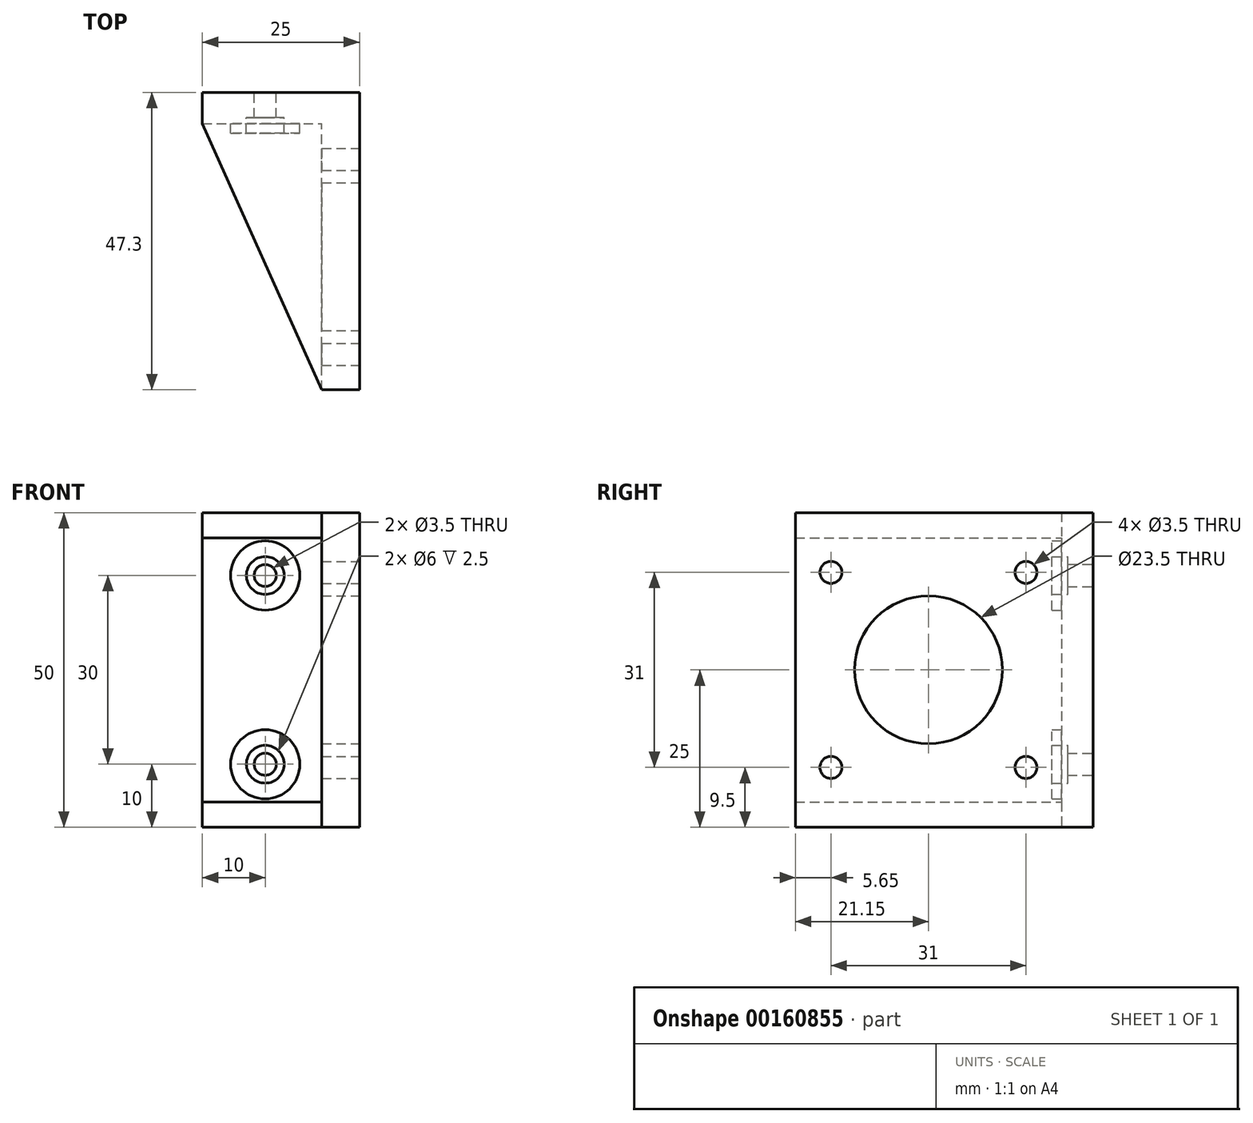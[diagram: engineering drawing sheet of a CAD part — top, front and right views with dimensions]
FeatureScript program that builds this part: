
annotation { "Feature Type Name" : "Feature", "Feature Type Description" : "" }
export const myFeature = defineFeature(function(context is Context, id is Id, definition is map)
    precondition{}
    {
        {
            var Q0;
            Q0=qCreatedBy(makeId("Front.planeOp"),FACE);
            var sketch = newSketch(context, id + "F0", { "sketchPlane" : qUnion([Q0])});
            skCircle(sketch, "E0", {"center": v(0, 15) * mm, "radius": 1.75 * mm});
            skCircle(sketch, "E1.MirrorC", {"center": v(0, -15) * mm, "radius": 1.75 * mm});
            skLineSegment(sketch, "E2.bottom", {"start": v(-10, 25) * mm, "end": v(15, 25) * mm});
            skLineSegment(sketch, "E2.top", {"start": v(-10, -25) * mm, "end": v(15, -25) * mm});
            skLineSegment(sketch, "E2.left", {"start": v(-10, 25) * mm, "end": v(-10, -25) * mm});
            skLineSegment(sketch, "E2.right", {"start": v(15, 25) * mm, "end": v(15, -25) * mm});
            skLineSegment(sketch, "E3", {"start": v(-10, 0) * mm, "end": v(0, 0) * mm});
            skPoint(sketch, "E4.visualSharp", {"position": v(-10, 25) * mm});
            skPoint(sketch, "E5.visualSharp", {"position": v(-10, -25) * mm});
            skSolve(sketch);
        }
        {
            var Q0;
            Q0 = qSketchRegion(id + "F0", true);
            extrude(context, id + "F1", {"entities" : qUnion([Q0]), "depth" : 5 * mm, "offsetDistance" : 25 * mm});
        }
        {
            var Q0;
            Q0=makeQuery(id+"F1.opExtrude","SWEPT_FACE",FACE,{"disambiguationData":[OSD([sQuery(id+"F0.wireOp",EDGE,"E2.right")])]});
            var sketch = newSketch(context, id + "F2", { "sketchPlane" : qUnion([Q0])});
            skLineSegment(sketch, "E6.bottom", {"start": v(-47.3, 25) * mm, "end": v(-5, 25) * mm});
            skLineSegment(sketch, "E6.top", {"start": v(-47.3, -25) * mm, "end": v(-5, -25) * mm});
            skLineSegment(sketch, "E6.left", {"start": v(-47.3, 25) * mm, "end": v(-47.3, -25) * mm});
            skLineSegment(sketch, "E6.right", {"start": v(-5, 25) * mm, "end": v(-5, -25) * mm});
            skLineSegment(sketch, "E7", {"start": v(-5, 0) * mm, "end": v(0, 0) * mm});
            skCircle(sketch, "E8", {"center": v(-26.15, 0) * mm, "radius": 11.75 * mm});
            skLineSegment(sketch, "E9", {"start": v(-47.3, 0) * mm, "end": v(-5, 0) * mm, "construction": true});
            skCircle(sketch, "E10", {"center": v(-10.65, 15.5) * mm, "radius": 1.75 * mm});
            skLineSegment(sketch, "E11", {"start": v(-26.15, 0) * mm, "end": v(-26.15, 11.75) * mm, "construction": true});
            skCircle(sketch, "E12.MirrorC", {"center": v(-41.65, 15.5) * mm, "radius": 1.75 * mm});
            skCircle(sketch, "E13.MirrorC", {"center": v(-10.65, -15.5) * mm, "radius": 1.75 * mm});
            skCircle(sketch, "E14.MirrorC", {"center": v(-41.65, -15.5) * mm, "radius": 1.75 * mm});
            skLineSegment(sketch, "E15", {"start": v(-26.15, 0) * mm, "end": v(-10.65, 15.5) * mm, "construction": true});
            skLineSegment(sketch, "E16", {"start": v(-41.65, 15.5) * mm, "end": v(-26.15, 0) * mm, "construction": true});
            skSolve(sketch);
        }
        {
            var Q0;
            Q0 = qSketchRegion(id + "F2", true);
            extrude(context, id + "F3", {"entities" : qUnion([Q0]), "operationType" : NewBodyOperationType.ADD, "oppositeDirection" : true, "depth" : 6 * mm, "offsetDistance" : 25 * mm});
        }
        {
            var Q0;
            Q0=makeQuery(id+"F3.boolean.opBoolean","MERGE",FACE,{"derivedFrom":[makeQuery(id+"F1.opExtrude","SWEPT_FACE",FACE,{"disambiguationData":[OSD([sQuery(id+"F0.wireOp",EDGE,"E2.top")])]}),makeQuery(id+"F3.opExtrude","SWEPT_FACE",FACE,{"disambiguationData":[OSD([sQuery(id+"F2.wireOp",EDGE,"E6.top")])]})]});
            var sketch = newSketch(context, id + "F4", { "sketchPlane" : qUnion([Q0])});
            skLineSegment(sketch, "E17", {"start": v(-10, 5) * mm, "end": v(9, 47.3) * mm});
            skLineSegment(sketch, "E18", {"start": v(9, 47.3) * mm, "end": v(9, 5) * mm});
            skLineSegment(sketch, "E19", {"start": v(9, 5) * mm, "end": v(-10, 5) * mm});
            skSolve(sketch);
        }
        {
            var Q0;
            Q0 = qSketchRegion(id + "F4", true);
            extrude(context, id + "F5", {"entities" : qUnion([Q0]), "operationType" : NewBodyOperationType.ADD, "oppositeDirection" : true, "depth" : 4 * mm, "offsetDistance" : 25 * mm});
        }
        {
            var Q0;
            Q0=makeQuery(id+"F3.boolean.opBoolean","MERGE",FACE,{"derivedFrom":[makeQuery(id+"F1.opExtrude","SWEPT_FACE",FACE,{"disambiguationData":[OSD([sQuery(id+"F0.wireOp",EDGE,"E2.bottom")])]}),makeQuery(id+"F3.opExtrude","SWEPT_FACE",FACE,{"disambiguationData":[OSD([sQuery(id+"F2.wireOp",EDGE,"E6.bottom")])]})]});
            var sketch = newSketch(context, id + "F6", { "sketchPlane" : qUnion([Q0])});
            skLineSegment(sketch, "E20", {"start": v(9, -47.3) * mm, "end": v(9, -5) * mm});
            skLineSegment(sketch, "E21", {"start": v(9, -5) * mm, "end": v(-10, -5) * mm});
            skLineSegment(sketch, "E22", {"start": v(-10, -5) * mm, "end": v(9, -47.3) * mm});
            skSolve(sketch);
        }
        {
            var Q0;
            Q0 = qSketchRegion(id + "F6", true);
            extrude(context, id + "F7", {"entities" : qUnion([Q0]), "operationType" : NewBodyOperationType.ADD, "oppositeDirection" : true, "depth" : 4 * mm, "offsetDistance" : 25 * mm});
        }
        {
            var Q0;
            Q0=makeQuery(id+"F1.opExtrude","CAP_FACE",FACE,{"disambiguationData":[OSD([sQuery(id+"F0.wireOp",EDGE,"E0"),sQuery(id+"F0.wireOp",EDGE,"E1.MirrorC"),sQuery(id+"F0.wireOp",EDGE,"E2.bottom"),sQuery(id+"F0.wireOp",EDGE,"E2.top"),sQuery(id+"F0.wireOp",EDGE,"E2.left"),sQuery(id+"F0.wireOp",EDGE,"E2.right")])],"isStart":false});
            var sketch = newSketch(context, id + "F8", { "sketchPlane" : qUnion([Q0])});
            skCircle(sketch, "E23", {"center": v(0, 15) * mm, "radius": 3 * mm});
            skCircle(sketch, "E24", {"center": v(0, 15) * mm, "radius": 5.5 * mm});
            skCircle(sketch, "E25.MirrorC", {"center": v(0, -15) * mm, "radius": 5.5 * mm});
            skCircle(sketch, "E26.MirrorC", {"center": v(0, -15) * mm, "radius": 3 * mm});
            skSolve(sketch);
        }
        {
            var Q0;
            Q0 = qSketchRegion(id + "F8", true);
            extrude(context, id + "F9", {"entities" : qUnion([Q0]), "operationType" : NewBodyOperationType.ADD, "depth" : 1.5 * mm, "offsetDistance" : 25 * mm});
        }
        {
            var Q0;
            {var subQ0=sQuery(id+"F0.wireOp",EDGE,"E0");Q0=makeQuery(id+"F9.boolean.opBoolean","SPLIT",FACE,{"disambiguationData":[TD([makeQuery(id+"F1.opExtrude","SWEPT_FACE",FACE,{"disambiguationData":[OSD([subQ0])]})])],"derivedFrom":makeQuery(id+"F1.opExtrude","CAP_FACE",FACE,{"disambiguationData":[OSD([subQ0,sQuery(id+"F0.wireOp",EDGE,"E1.MirrorC"),sQuery(id+"F0.wireOp",EDGE,"E2.bottom"),sQuery(id+"F0.wireOp",EDGE,"E2.top"),sQuery(id+"F0.wireOp",EDGE,"E2.left"),sQuery(id+"F0.wireOp",EDGE,"E2.right")])],"isStart":false})});}
            var Q1;
            {var subQ0=sQuery(id+"F0.wireOp",EDGE,"E1.MirrorC");Q1=makeQuery(id+"F9.boolean.opBoolean","SPLIT",FACE,{"disambiguationData":[TD([makeQuery(id+"F1.opExtrude","SWEPT_FACE",FACE,{"disambiguationData":[OSD([subQ0])]})])],"derivedFrom":makeQuery(id+"F1.opExtrude","CAP_FACE",FACE,{"disambiguationData":[OSD([sQuery(id+"F0.wireOp",EDGE,"E0"),subQ0,sQuery(id+"F0.wireOp",EDGE,"E2.bottom"),sQuery(id+"F0.wireOp",EDGE,"E2.top"),sQuery(id+"F0.wireOp",EDGE,"E2.left"),sQuery(id+"F0.wireOp",EDGE,"E2.right")])],"isStart":false})});}
            extrude(context, id + "F10", {"entities" : qUnion([Q0, Q1]), "operationType" : NewBodyOperationType.REMOVE, "oppositeDirection" : true, "depth" : 1 * mm, "offsetDistance" : 25 * mm});
        }
    });
